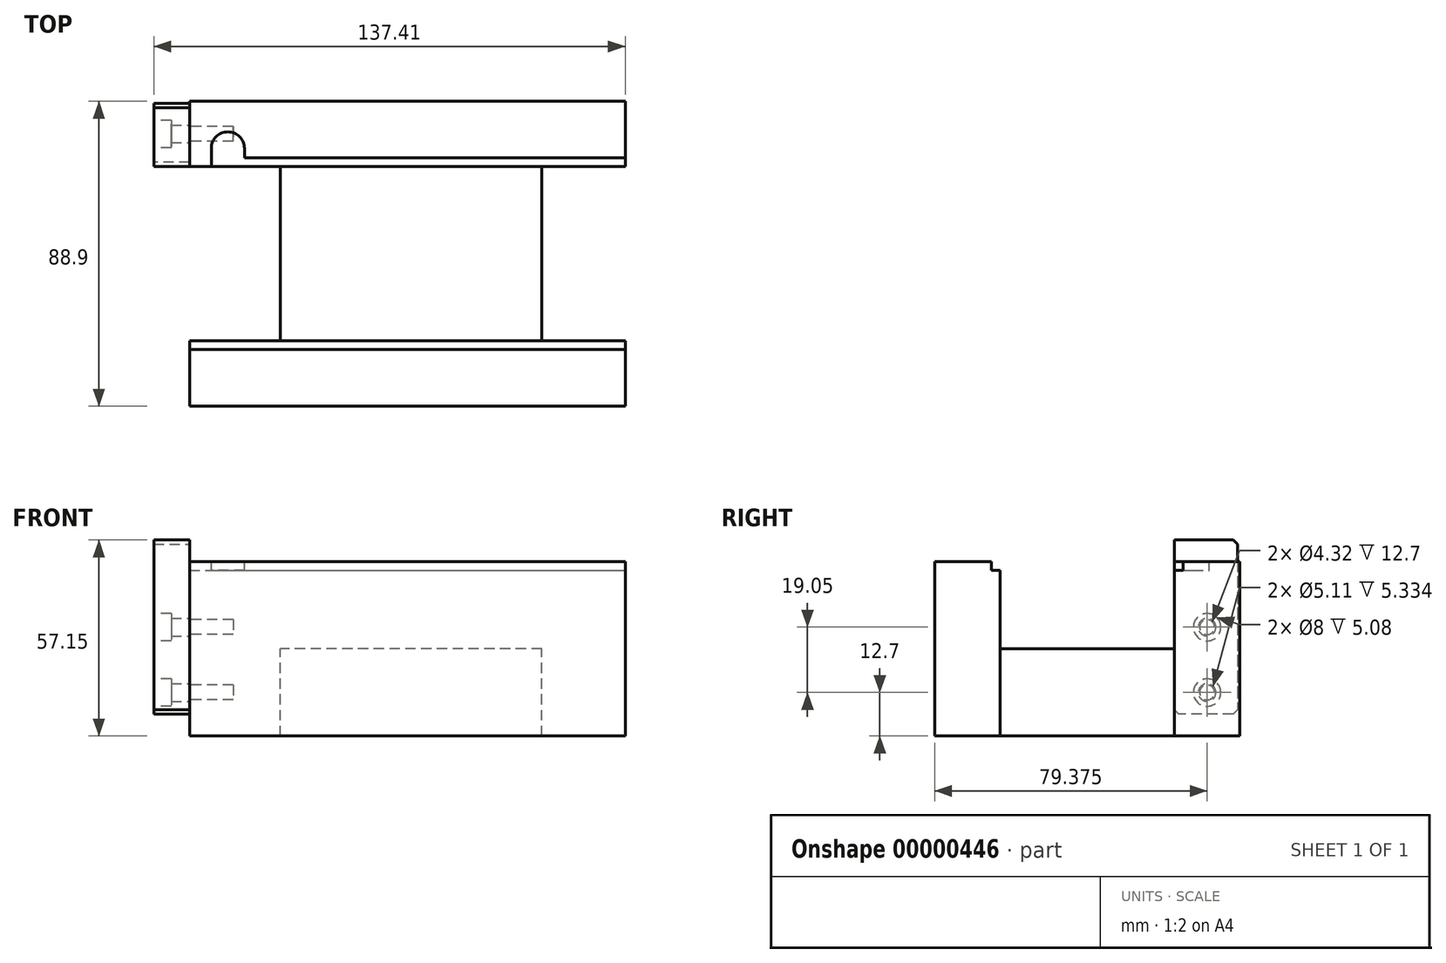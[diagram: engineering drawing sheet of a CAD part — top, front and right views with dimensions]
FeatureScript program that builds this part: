
annotation { "Feature Type Name" : "Feature", "Feature Type Description" : "" }
export const myFeature = defineFeature(function(context is Context, id is Id, definition is map)
    precondition{}
    {
        {
            var Q0;
            Q0=qCreatedBy(makeId("Top.planeOp"),FACE);
            var sketch = newSketch(context, id + "F0", { "sketchPlane" : qUnion([Q0])});
            skLineSegment(sketch, "E0.bottom", {"start": v(0, 0) * mm, "end": v(127, 0) * mm});
            skLineSegment(sketch, "E0.top", {"start": v(0, 19.05) * mm, "end": v(127, 19.05) * mm});
            skLineSegment(sketch, "E0.left", {"start": v(0, 0) * mm, "end": v(0, 19.05) * mm});
            skLineSegment(sketch, "E0.right", {"start": v(127, 0) * mm, "end": v(127, 19.05) * mm});
            skSolve(sketch);
        }
        {
            var Q0;
            Q0 = qSketchRegion(id + "F0", true);
            extrude(context, id + "F1", {"entities" : qUnion([Q0]), "depth" : 50.8 * mm});
        }
        {
            var Q0;
            Q0=makeQuery(id+"F1.opExtrude","SWEPT_FACE",FACE,{"disambiguationData":[OSD([sQuery(id+"F0.wireOp",EDGE,"E0.top")])]});
            var sketch = newSketch(context, id + "F2", { "sketchPlane" : qUnion([Q0])});
            skLineSegment(sketch, "E1.bottom", {"start": v(-102.71, 0) * mm, "end": v(-26.51, 0) * mm});
            skLineSegment(sketch, "E1.top", {"start": v(-102.71, 25.4) * mm, "end": v(-26.51, 25.4) * mm});
            skLineSegment(sketch, "E1.left", {"start": v(-102.71, 0) * mm, "end": v(-102.71, 25.4) * mm});
            skLineSegment(sketch, "E1.right", {"start": v(-26.51, 0) * mm, "end": v(-26.51, 25.4) * mm});
            skSolve(sketch);
        }
        {
            var Q0;
            Q0 = qSketchRegion(id + "F2", true);
            extrude(context, id + "F3", {"entities" : qUnion([Q0]), "depth" : 50.8 * mm});
        }
        {
            var Q0;
            Q0=qCreatedBy(makeId("Top.planeOp"),FACE);
            var sketch = newSketch(context, id + "F4", { "sketchPlane" : qUnion([Q0])});
            skLineSegment(sketch, "E2.bottom", {"start": v(0, 69.85) * mm, "end": v(127, 69.85) * mm});
            skLineSegment(sketch, "E2.top", {"start": v(0, 88.9) * mm, "end": v(127, 88.9) * mm});
            skLineSegment(sketch, "E2.left", {"start": v(0, 69.85) * mm, "end": v(0, 88.9) * mm});
            skLineSegment(sketch, "E2.right", {"start": v(127, 69.85) * mm, "end": v(127, 88.9) * mm});
            skSolve(sketch);
        }
        {
            var Q0;
            Q0 = qSketchRegion(id + "F4", true);
            extrude(context, id + "F5", {"entities" : qUnion([Q0]), "depth" : 50.8 * mm});
        }
        {
            var Q0;
            Q0=makeQuery(id+"F1.opExtrude","CAP_FACE",FACE,{"disambiguationData":[OSD([sQuery(id+"F0.wireOp",EDGE,"E0.bottom"),sQuery(id+"F0.wireOp",EDGE,"E0.top"),sQuery(id+"F0.wireOp",EDGE,"E0.left"),sQuery(id+"F0.wireOp",EDGE,"E0.right")])],"isStart":false});
            var sketch = newSketch(context, id + "F6", { "sketchPlane" : qUnion([Q0])});
            skLineSegment(sketch, "E3.bottom", {"start": v(0, 19.05) * mm, "end": v(127, 19.05) * mm});
            skLineSegment(sketch, "E3.top", {"start": v(0, 16.5) * mm, "end": v(127, 16.5) * mm});
            skLineSegment(sketch, "E3.left", {"start": v(0, 19.05) * mm, "end": v(0, 16.5) * mm});
            skLineSegment(sketch, "E3.right", {"start": v(127, 19.05) * mm, "end": v(127, 16.5) * mm});
            skSolve(sketch);
        }
        {
            var Q0;
            Q0 = qSketchRegion(id + "F6", true);
            extrude(context, id + "F7", {"entities" : qUnion([Q0]), "operationType" : NewBodyOperationType.REMOVE, "oppositeDirection" : true, "depth" : 2.54 * mm});
        }
        {
            var Q0;
            Q0=makeQuery(id+"F5.opExtrude","CAP_FACE",FACE,{"disambiguationData":[OSD([sQuery(id+"F4.wireOp",EDGE,"E2.bottom"),sQuery(id+"F4.wireOp",EDGE,"E2.top"),sQuery(id+"F4.wireOp",EDGE,"E2.left"),sQuery(id+"F4.wireOp",EDGE,"E2.right")])],"isStart":false});
            var sketch = newSketch(context, id + "F8", { "sketchPlane" : qUnion([Q0])});
            skLineSegment(sketch, "E4.bottom", {"start": v(6.35, 69.85) * mm, "end": v(127, 69.85) * mm});
            skLineSegment(sketch, "E4.right", {"start": v(127, 69.85) * mm, "end": v(127, 72.4) * mm});
            skLineSegment(sketch, "E5.bottom", {"start": v(16, 69.85) * mm, "end": v(6.35, 69.85) * mm});
            skLineSegment(sketch, "E5.top", {"start": v(11.18, 80.01) * mm, "end": v(11.18, 80.01) * mm});
            skLineSegment(sketch, "E5.left", {"start": v(16, 72.39) * mm, "end": v(16, 75.18) * mm});
            skLineSegment(sketch, "E5.right", {"start": v(6.35, 69.85) * mm, "end": v(6.35, 75.18) * mm});
            skLineSegment(sketch, "E6.trimOffspring", {"start": v(16, 72.4) * mm, "end": v(127, 72.4) * mm});
            skPoint(sketch, "E7.visualSharp", {"position": v(16, 80.01) * mm});
            skArc(sketch, "E7.filletArc", {"start": v(16, 75.18) * mm, "mid": v(14.59, 78.6) * mm, "end": v(11.18, 80.01) * mm});
            skPoint(sketch, "E8.visualSharp", {"position": v(6.35, 80.01) * mm});
            skArc(sketch, "E8.filletArc", {"start": v(11.18, 80.01) * mm, "mid": v(7.76, 78.6) * mm, "end": v(6.35, 75.18) * mm});
            skSolve(sketch);
        }
        {
            var Q0;
            Q0 = qSketchRegion(id + "F8", true);
            extrude(context, id + "F9", {"entities" : qUnion([Q0]), "operationType" : NewBodyOperationType.REMOVE, "oppositeDirection" : true, "depth" : 2.54 * mm});
        }
        {
            var Q0;
            Q0=makeQuery(id+"F5.opExtrude","SWEPT_FACE",FACE,{"disambiguationData":[OSD([sQuery(id+"F4.wireOp",EDGE,"E2.left")])]});
            var sketch = newSketch(context, id + "F10", { "sketchPlane" : qUnion([Q0])});
            skCircle(sketch, "E9", {"center": v(-79.38, 31.75) * mm, "radius": 2.16 * mm});
            skCircle(sketch, "E10", {"center": v(-79.38, 12.7) * mm, "radius": 2.16 * mm});
            skSolve(sketch);
        }
        {
            var Q0;
            Q0 = qSketchRegion(id + "F10", true);
            extrude(context, id + "F11", {"entities" : qUnion([Q0]), "operationType" : NewBodyOperationType.REMOVE, "oppositeDirection" : true, "depth" : 12.7 * mm, "offsetDistance" : 25.4 * mm});
        }
        {
            var Q0;
            Q0=makeQuery(id+"F5.opExtrude","SWEPT_FACE",FACE,{"disambiguationData":[OSD([sQuery(id+"F4.wireOp",EDGE,"E2.left")])]});
            var sketch = newSketch(context, id + "F12", { "sketchPlane" : qUnion([Q0])});
            skLineSegment(sketch, "E11.0", {"start": v(-69.85, 57.15) * mm, "end": v(-88.27, 57.15) * mm});
            skLineSegment(sketch, "E12.0", {"start": v(-69.85, 57.15) * mm, "end": v(-69.85, 6.35) * mm});
            skLineSegment(sketch, "E13.0", {"start": v(-88.27, 57.15) * mm, "end": v(-88.27, 6.35) * mm});
            skLineSegment(sketch, "E14", {"start": v(-88.27, 6.35) * mm, "end": v(-69.85, 6.35) * mm});
            skCircle(sketch, "E15", {"center": v(-79.38, 12.7) * mm, "radius": 2.55 * mm});
            skCircle(sketch, "E16", {"center": v(-79.38, 31.75) * mm, "radius": 2.55 * mm});
            skSolve(sketch);
        }
        {
            var Q0;
            Q0 = qSketchRegion(id + "F12", true);
            extrude(context, id + "F13", {"entities" : qUnion([Q0]), "depth" : 10.4 * mm, "offsetDistance" : 25.4 * mm});
        }
        {
            var Q0;
            Q0=makeQuery(id+"F13.opExtrude","SWEPT_EDGE",EDGE,{"disambiguationData":[OSD([sQuery(id+"F4.wireOp",EDGE,"E2.top"),sQuery(id+"F4.wireOp",EDGE,"E2.left"),sQuery(id+"F12.wireOp",EDGE,"E13.0"),sQuery(id+"F12.wireOp",EDGE,"E14")])]});
            var Q1;
            Q1=makeQuery(id+"F13.opExtrude","SWEPT_EDGE",EDGE,{"disambiguationData":[OSD([sQuery(id+"F12.wireOp",EDGE,"E11.0"),sQuery(id+"F12.wireOp",EDGE,"E13.0")])]});
            var Q2;
            Q2=makeQuery(id+"F13.opExtrude","SWEPT_EDGE",EDGE,{"disambiguationData":[OSD([sQuery(id+"F4.wireOp",EDGE,"E2.bottom"),sQuery(id+"F4.wireOp",EDGE,"E2.left"),sQuery(id+"F12.wireOp",EDGE,"E12.0"),sQuery(id+"F12.wireOp",EDGE,"E14")])]});
            chamfer(context, id + "F14", {"entities" : qUnion([Q0, Q1, Q2]), "width" : 1.27 * mm, "tangentPropagation" : true});
        }
        {
            var Q0;
            Q0=makeQuery(id+"F13.opExtrude","CAP_FACE",FACE,{"disambiguationData":[OSD([sQuery(id+"F12.wireOp",EDGE,"E11.0"),sQuery(id+"F12.wireOp",EDGE,"E12.0"),sQuery(id+"F12.wireOp",EDGE,"E13.0"),sQuery(id+"F12.wireOp",EDGE,"E14"),sQuery(id+"F12.wireOp",EDGE,"E15"),sQuery(id+"F12.wireOp",EDGE,"E16")])],"isStart":false});
            var sketch = newSketch(context, id + "F15", { "sketchPlane" : qUnion([Q0])});
            skCircle(sketch, "E17", {"center": v(-79.38, 31.75) * mm, "radius": 4 * mm});
            skCircle(sketch, "E18", {"center": v(-79.38, 12.7) * mm, "radius": 4 * mm});
            skSolve(sketch);
        }
        {
            var Q0;
            Q0 = qSketchRegion(id + "F15", true);
            extrude(context, id + "F16", {"entities" : qUnion([Q0]), "operationType" : NewBodyOperationType.REMOVE, "oppositeDirection" : true, "depth" : 5.08 * mm, "offsetDistance" : 25.4 * mm});
        }
    });
